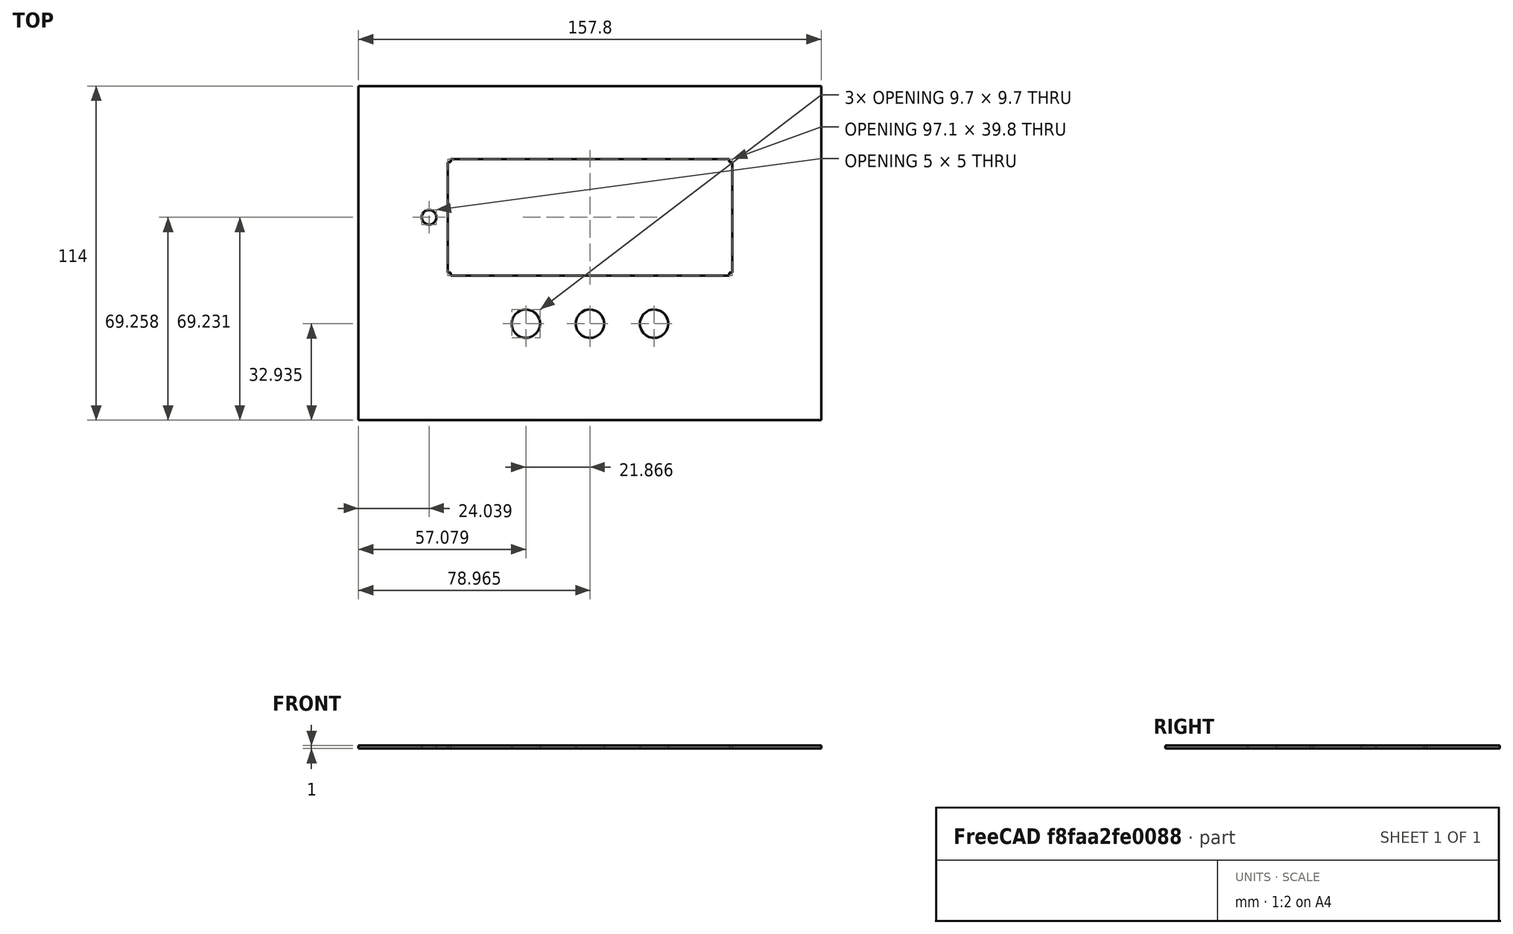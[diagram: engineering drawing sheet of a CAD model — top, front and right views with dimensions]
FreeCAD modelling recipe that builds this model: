
FCSTD DOCUMENT  (FreeCAD 0.19R24276 (Git))
Label: cnc
License: All rights reserved
LicenseURL: http://en.wikipedia.org/wiki/All_rights_reserved
objects: Sketcher::SketchObject×3, PartDesign::Pocket×2, PartDesign::Pad×1, PartDesign::Body×1, Part::Part2DObjectPython×1
note: 11 computed .brp shape members not serialized (recipe doc carries the construction recipe); baked Part::Feature solids carry a one-line shape summary decoded from their .brp

FEATURE [Sketcher::SketchObject] Sketch  label="bottom"
  FullyConstrained = true
  MapMode = 5
  Support = -> [XY_Plane]
  sketch-geometry (4):
    g0: LineSegment StartX=-78.9 StartY=76 StartZ=0 EndX=78.9 EndY=76 EndZ=0
    g1: LineSegment StartX=78.9 StartY=76 StartZ=0 EndX=78.9 EndY=-38 EndZ=0
    g2: LineSegment StartX=78.9 StartY=-38 StartZ=0 EndX=-78.9 EndY=-38 EndZ=0
    g3: LineSegment StartX=-78.9 StartY=-38 StartZ=0 EndX=-78.9 EndY=76 EndZ=0
  constraints (13):
    c: Horizontal(g0)
    c: Horizontal(g2)
    c: Vertical(g1)
    c: Vertical(g3)
    c: DistanceX(g3,g-1) = 78.9
    c: DistanceX(g-1,g1) = 78.9
    c: Coincident(g2,g3)
    c: Coincident(g0,g3)
    c: Coincident(g0,g1)
    c: DistanceY(g-1,g0) = 76
    c: DistanceY(g1,g-1) = 38
    c: DistanceY(g2,g-1) = 38
    c: DistanceX(g-1,g2) = 78.9
FEATURE [PartDesign::Pad] Pad  label="bottom_pad"
  Direction = (1,1,1)
  Length = 1
  Length2 = 100
  Profile = -> Sketch
  Type = 0
FEATURE [Sketcher::SketchObject] Sketch013  label="led_holes"
  AttachmentOffset = pos=(0,15,0) rot=(0,0,1;0rad)
  FullyConstrained = false
  MapMode = 5
  Placement = pos=(0,15,1) rot=(0,0,1;0rad)
  sketch-geometry (4):
    g0: BSplineCurve PolesCount=7 KnotsCount=4 Degree=2 IsPeriodic=0
    g1: BSplineCurve PolesCount=7 KnotsCount=4 Degree=2 IsPeriodic=0
    g2: BSplineCurve PolesCount=7 KnotsCount=4 Degree=2 IsPeriodic=0
    g3: BSplineCurve PolesCount=7 KnotsCount=4 Degree=2 IsPeriodic=0
FEATURE [Sketcher::SketchObject] Sketch026  label="display_hole"
  AttachmentOffset = pos=(0,15,0) rot=(0,0,1;0rad)
  FullyConstrained = false
  MapMode = 5
  Placement = pos=(0,15,1) rot=(0,0,1;0rad)
  Support = -> [Pad]
  sketch-geometry (12):
    g0: BSplineCurve PolesCount=2 KnotsCount=2 Degree=1 IsPeriodic=0
    g1: BSplineCurve PolesCount=2 KnotsCount=2 Degree=1 IsPeriodic=0
    g2: BSplineCurve PolesCount=2 KnotsCount=2 Degree=1 IsPeriodic=0
    g3: BSplineCurve PolesCount=2 KnotsCount=2 Degree=1 IsPeriodic=0
    g4: BSplineCurve PolesCount=2 KnotsCount=2 Degree=1 IsPeriodic=0
    g5: BSplineCurve PolesCount=2 KnotsCount=2 Degree=1 IsPeriodic=0
    g6: BSplineCurve PolesCount=2 KnotsCount=2 Degree=1 IsPeriodic=0
    g7: BSplineCurve PolesCount=2 KnotsCount=2 Degree=1 IsPeriodic=0
    g8: BSplineCurve PolesCount=2 KnotsCount=2 Degree=1 IsPeriodic=0
    g9: BSplineCurve PolesCount=2 KnotsCount=2 Degree=1 IsPeriodic=0
    g10: BSplineCurve PolesCount=2 KnotsCount=2 Degree=1 IsPeriodic=0
    g11: BSplineCurve PolesCount=2 KnotsCount=2 Degree=1 IsPeriodic=0
FEATURE [PartDesign::Pocket] Pocket001  label="display_hole_pocket"
  BaseFeature = -> Pad
  Length = 5
  Length2 = 100
  Profile = -> Sketch026
  Type = 1
FEATURE [PartDesign::Pocket] Pocket002  label="led_holes_pocket"
  BaseFeature = -> Pocket001
  Length = 5
  Length2 = 100
  Profile = -> Sketch013
  Type = 1
FEATURE [PartDesign::Body] Body
  Group = -> [Sketch,Pad,Sketch026,Pocket001,Sketch013,Pocket002]
  Origin = -> Origin
  Tip = -> Pocket002
FEATURE [Part::Part2DObjectPython] Shape2DView  # Draft 2D object (typed FeaturePython)
  Base = -> Pocket002
  FuseArch = false
  HiddenLines = false
  InPlace = true
  Projection = (0,0,1)
  ProjectionMode = 0
  SegmentLength = 0.05
  Tessellation = false
  VisibleOnly = false
